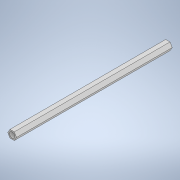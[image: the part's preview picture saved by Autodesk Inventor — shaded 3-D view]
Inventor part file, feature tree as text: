
AUTODESK INVENTOR PART (.ipt)
format: ipt  version: 2022.2 (Build 262287010, 287A)  size: 115,712 bytes
history: native  units: in
note: dims shown in document units (in); Inventor stores cm internally (conversion verified against a paired STEP export)
features: sketch x3, hole x2, extrude x1
ambient origin geometry x8: Origin, YZ Plane, XZ Plane, XY Plane, X Axis, Y Axis, Z Axis, Center Point
bodies: Body1 (feature_tree)
feature tree (6):
  extrude  "Extrusion2"  Depth=0.375in
  hole  "Hole1"  [1 undecoded]
  hole  "Hole2"  [1 undecoded]
  sketch  "Sketch1"  dims[d0=0.375in d3=0.159in]
  sketch  "Sketch2"  dims[d4=7.75in d5=0.0in]
  sketch  "Sketch3"  dims[d6=0.24in d7=0.75in d8=0.27in d9=0.2411in d10=0.5635in d11=0.31in d12=0.0in d13=0.24in d14=0.75in d15=0.27in d16=0.2411in d17=0.5635in d18=0.31in d19=0.0in]
note: 2 required parameter values undecoded (feature->parameter linkage not recoverable at this tier; creation-order binding heuristic only, values carry confidence <= 0.55)
